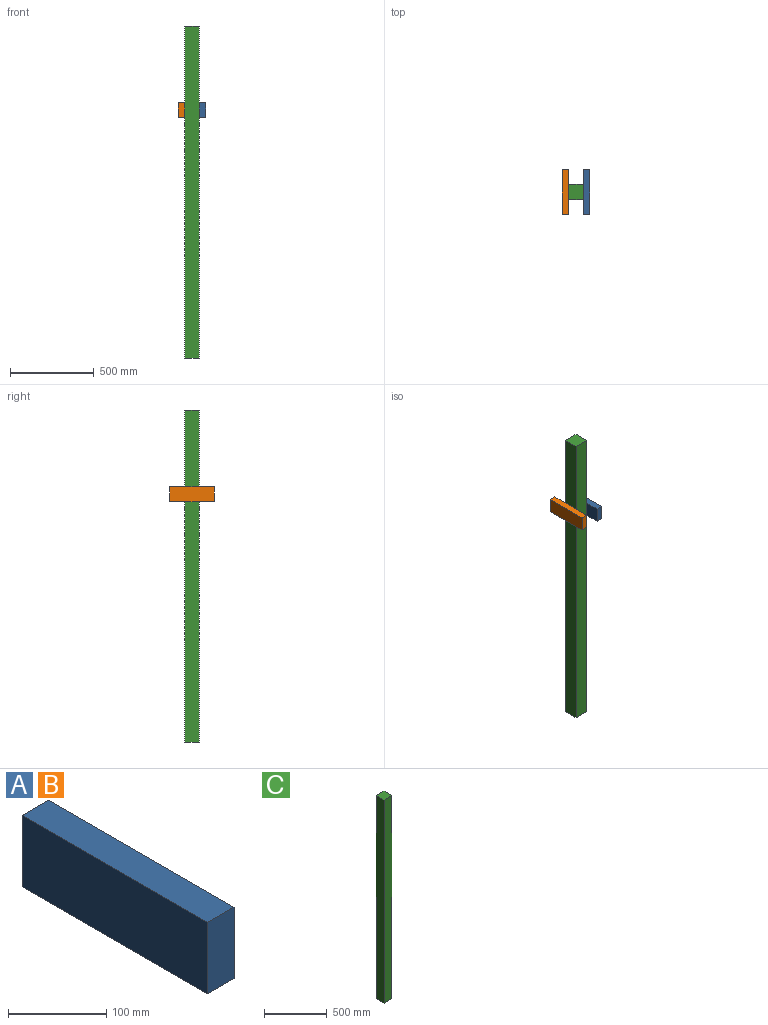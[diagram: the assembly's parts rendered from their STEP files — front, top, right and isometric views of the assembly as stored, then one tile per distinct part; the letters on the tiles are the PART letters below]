
ASSEMBLY  parts=3 mates=2
PART A: 6 faces, bbox 38.1x266.7x88.9 mm
  f0: plane 266.7x38.1mm, normal (0,0,1), area 10161.3mm2, adj f1,f3,f4,f5
  f1: plane 266.7x88.9mm, normal (-1,0,0), area 23709.6mm2, adj f0,f2,f4,f5
  f2: plane 266.7x38.1mm, normal (0,0,-1), area 10161.3mm2, adj f1,f3,f4,f5
  f3: plane 266.7x88.9mm, normal (1,0,0), area 23709.6mm2, adj f0,f2,f4,f5
  f4: plane 88.9x38.1mm, normal (0,-1,0), area 3387.1mm2, adj f0,f1,f2,f3
  f5: plane 88.9x38.1mm, normal (0,1,0), area 3387.1mm2, adj f0,f1,f2,f3
PART B: same geometry as A
PART C: 6 faces, bbox 88.9x88.9x1981.2 mm
  f0: plane 1981.2x88.9mm, normal (0,1,0), area 176128.7mm2, adj f1,f3,f4,f5
  f1: plane 1981.2x88.9mm, normal (-1,0,0), area 176128.7mm2, adj f0,f2,f4,f5
  f2: plane 1981.2x88.9mm, normal (0,-1,0), area 176128.7mm2, adj f1,f3,f4,f5
  f3: plane 1981.2x88.9mm, normal (1,0,0), area 176128.7mm2, adj f0,f2,f4,f5
  f4: plane 88.9x88.9mm, normal (0,0,1), area 7903.2mm2, adj f0,f1,f2,f3
  f5: plane 88.9x88.9mm, normal (0,0,-1), area 7903.2mm2, adj f0,f1,f2,f3
PLACE A rot(axis=(0,0,1),180deg) t=(-1115.86,-247.37,1312.09)mm
PLACE B t=(-1193.05,19.33,1312.09)mm
PLACE C t=(-1161.38,-122.14,-161.85)mm
MATE fastened A.f3 <-> C.f3  axis (-1,0,0) through (-1110,-114.02,1362.15)mm
MATE fastened B.f3 <-> C.f1  axis (1,0,0) through (-1198.9,-114.02,1362.15)mm
